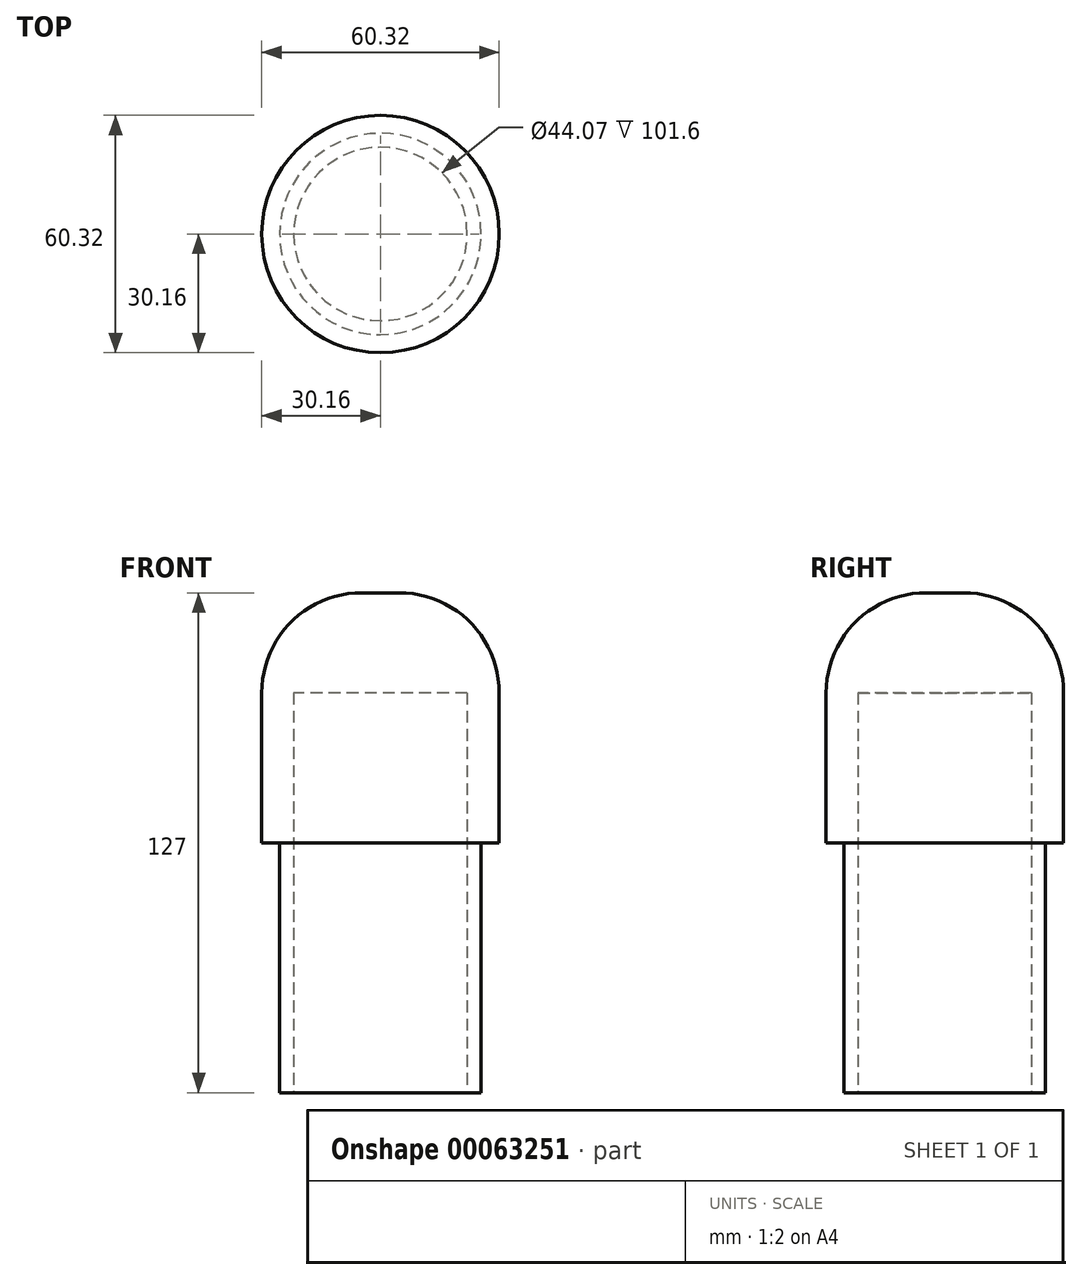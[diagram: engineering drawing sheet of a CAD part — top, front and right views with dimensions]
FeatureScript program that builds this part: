
annotation { "Feature Type Name" : "Feature", "Feature Type Description" : "" }
export const myFeature = defineFeature(function(context is Context, id is Id, definition is map)
    precondition{}
    {
        {
            var Q0;
            Q0=qCreatedBy(makeId("Top.planeOp"),FACE);
            var sketch = newSketch(context, id + "F0", { "sketchPlane" : qUnion([Q0])});
            skCircle(sketch, "E0", {"center": v(0, 0) * mm, "radius": 30.16 * mm});
            skSolve(sketch);
        }
        {
            var Q0;
            Q0=makeQuery(id+"F0.imprint","IMPRINT",FACE,{"disambiguationData":[TD([[makeQuery(id+"F0.imprint","IMPRINT",EDGE,{"derivedFrom":sQuery(id+"F0.wireOp",EDGE,"E0")}),1.0]])]});
            extrude(context, id + "F1", {"entities" : qUnion([Q0]), "depth" : 127 * mm});
        }
        {
            var Q0;
            Q0=makeQuery(id+"F1.opExtrude","CAP_EDGE",EDGE,{"disambiguationData":[OSD([sQuery(id+"F0.wireOp",EDGE,"E0")])],"isStart":false});
            fillet(context, id + "F2", {"entities" : qUnion([Q0]), "radius" : 25.4 * mm, "tangentPropagation" : true, "allowEdgeOverflow" : false});
        }
        {
            var Q0;
            Q0=makeQuery(id+"F0.imprint","IMPRINT",FACE,{"disambiguationData":[TD([[makeQuery(id+"F0.imprint","IMPRINT",EDGE,{"derivedFrom":sQuery(id+"F0.wireOp",EDGE,"E0")}),1.0]])]});
            var sketch = newSketch(context, id + "F3", { "sketchPlane" : qUnion([Q0])});
            skCircle(sketch, "E1.0", {"center": v(0, 0) * mm, "radius": 26.1 * mm});
            skCircle(sketch, "E2.0", {"center": v(0, 0) * mm, "radius": 22.03 * mm});
            skSolve(sketch);
        }
        {
            var Q0;
            Q0=makeQuery(id+"F3.imprint","IMPRINT",FACE,{"disambiguationData":[TD([[makeQuery(id+"F3.imprint","IMPRINT",EDGE,{"derivedFrom":sQuery(id+"F3.wireOp",EDGE,"E2.0")}),1.0]])]});
            extrude(context, id + "F4", {"entities" : qUnion([Q0]), "operationType" : NewBodyOperationType.REMOVE, "depth" : 101.6 * mm});
        }
        {
            var Q0;
            Q0=makeQuery(id+"F0.imprint","IMPRINT",FACE,{"disambiguationData":[TD([[makeQuery(id+"F0.imprint","IMPRINT",EDGE,{"derivedFrom":sQuery(id+"F0.wireOp",EDGE,"E0")}),1.0]])]});
            var sketch = newSketch(context, id + "F5", { "sketchPlane" : qUnion([Q0])});
            skCircle(sketch, "E3.0", {"center": v(0, 0) * mm, "radius": 25.6 * mm});
            skSolve(sketch);
        }
        {
            var Q0;
            Q0=makeQuery(id+"F5.imprint","IMPRINT",FACE,{"disambiguationData":[TD([[makeQuery(id+"F5.imprint","IMPRINT",EDGE,{"derivedFrom":sQuery(id+"F5.wireOp",EDGE,"E3.0")}),-1.0]])]});
            extrude(context, id + "F6", {"entities" : qUnion([Q0]), "operationType" : NewBodyOperationType.REMOVE, "depth" : 63.5 * mm});
        }
    });
